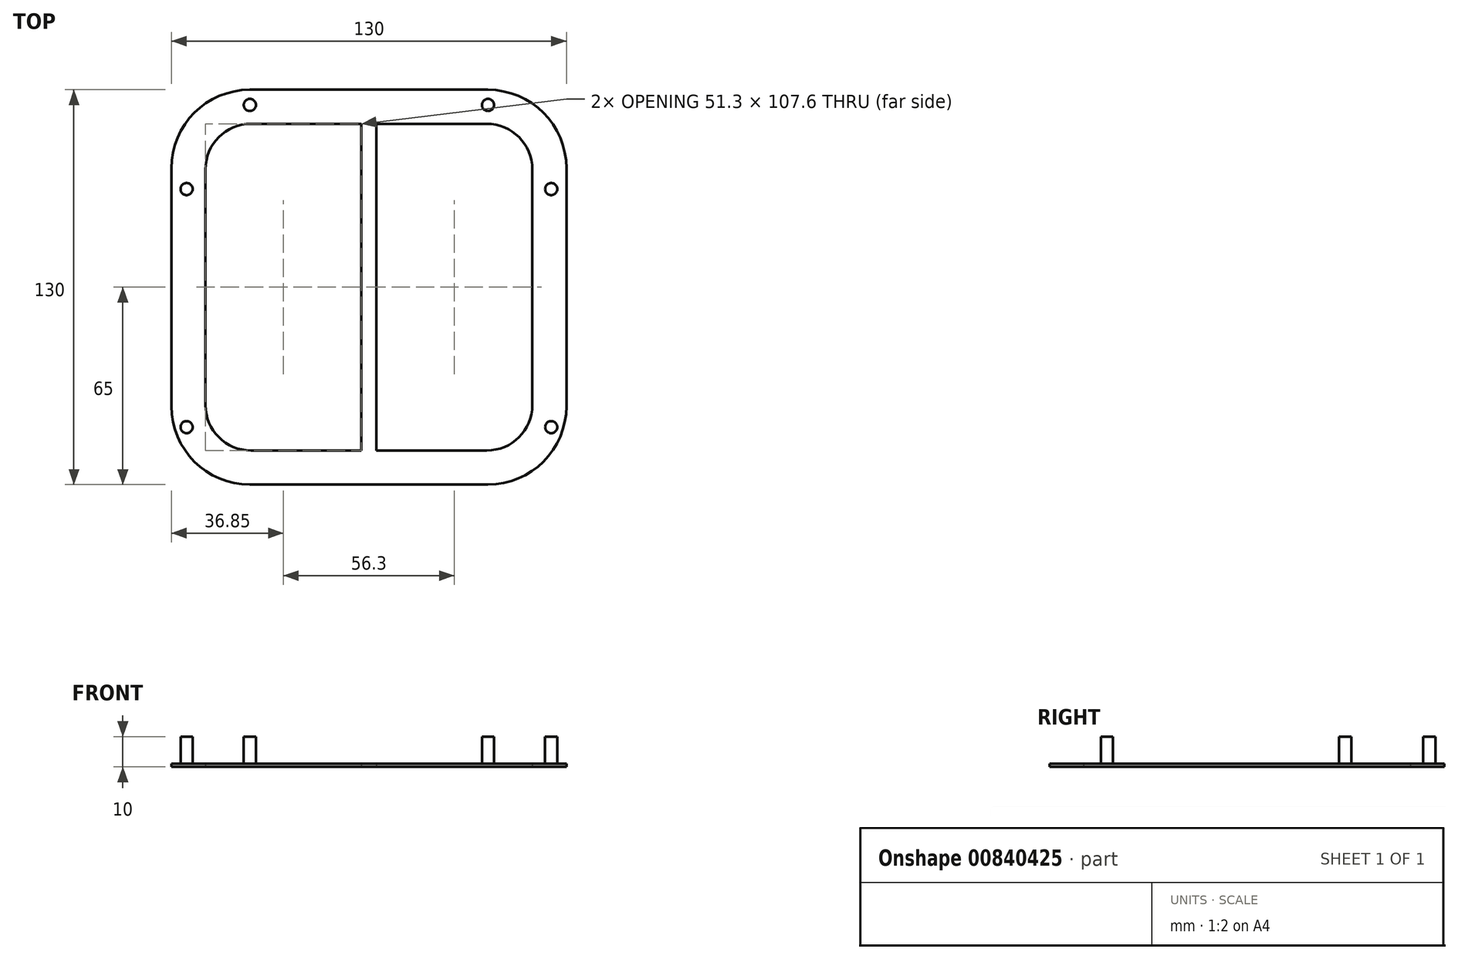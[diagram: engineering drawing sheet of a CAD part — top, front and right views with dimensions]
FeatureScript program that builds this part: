
annotation { "Feature Type Name" : "Feature", "Feature Type Description" : "" }
export const myFeature = defineFeature(function(context is Context, id is Id, definition is map)
    precondition{}
    {
        {
            var Q0;
            Q0=qCreatedBy(makeId("Top.planeOp"),FACE);
            var sketch = newSketch(context, id + "F0", { "sketchPlane" : qUnion([Q0])});
            skLineSegment(sketch, "E0.bottom", {"start": v(-39.2, 55) * mm, "end": v(39.2, 55) * mm});
            skLineSegment(sketch, "E0.top", {"start": v(-39.2, -55) * mm, "end": v(39.2, -55) * mm});
            skLineSegment(sketch, "E0.left", {"start": v(-55, 39.2) * mm, "end": v(-55, -39.2) * mm});
            skLineSegment(sketch, "E0.right", {"start": v(55, 39.2) * mm, "end": v(55, -39.2) * mm});
            skPoint(sketch, "E0.middle", {"position": v(0, 0) * mm});
            skLineSegment(sketch, "E1.bottom", {"start": v(39.2, 65) * mm, "end": v(-39.2, 65) * mm});
            skLineSegment(sketch, "E1.top", {"start": v(39.2, -65) * mm, "end": v(-39.2, -65) * mm});
            skLineSegment(sketch, "E1.left", {"start": v(65, 39.2) * mm, "end": v(65, -39.2) * mm});
            skLineSegment(sketch, "E1.right", {"start": v(-65, 39.2) * mm, "end": v(-65, -39.2) * mm});
            skLineSegment(sketch, "E2.0", {"start": v(-38.8, 53.8) * mm, "end": v(38.8, 53.8) * mm});
            skLineSegment(sketch, "E2.1", {"start": v(-53.8, 38.8) * mm, "end": v(-53.8, -38.8) * mm});
            skLineSegment(sketch, "E2.2", {"start": v(-38.8, -53.8) * mm, "end": v(38.8, -53.8) * mm});
            skLineSegment(sketch, "E2.3", {"start": v(53.8, 38.8) * mm, "end": v(53.8, -38.8) * mm});
            skPoint(sketch, "E3.visualSharp", {"position": v(-53.8, -53.8) * mm});
            skArc(sketch, "E3.filletArc", {"start": v(-53.8, -38.8) * mm, "mid": v(-49.4, -49.4) * mm, "end": v(-38.8, -53.8) * mm});
            skPoint(sketch, "E4.visualSharp", {"position": v(-55, -55) * mm});
            skArc(sketch, "E4.filletArc", {"start": v(-55, -39.2) * mm, "mid": v(-50.37, -50.37) * mm, "end": v(-39.2, -55) * mm});
            skPoint(sketch, "E5.visualSharp", {"position": v(53.8, -53.8) * mm});
            skArc(sketch, "E5.filletArc", {"start": v(38.8, -53.8) * mm, "mid": v(49.4, -49.4) * mm, "end": v(53.8, -38.8) * mm});
            skPoint(sketch, "E6.visualSharp", {"position": v(53.8, 53.8) * mm});
            skArc(sketch, "E6.filletArc", {"start": v(53.8, 38.8) * mm, "mid": v(49.4, 49.4) * mm, "end": v(38.8, 53.8) * mm});
            skPoint(sketch, "E7.visualSharp", {"position": v(-53.8, 53.8) * mm});
            skArc(sketch, "E7.filletArc", {"start": v(-38.8, 53.8) * mm, "mid": v(-49.4, 49.4) * mm, "end": v(-53.8, 38.8) * mm});
            skPoint(sketch, "E8.visualSharp", {"position": v(-55, 55) * mm});
            skArc(sketch, "E8.filletArc", {"start": v(-39.2, 55) * mm, "mid": v(-50.37, 50.37) * mm, "end": v(-55, 39.2) * mm});
            skPoint(sketch, "E9.visualSharp", {"position": v(55, 55) * mm});
            skArc(sketch, "E9.filletArc", {"start": v(55, 39.2) * mm, "mid": v(50.37, 50.37) * mm, "end": v(39.2, 55) * mm});
            skPoint(sketch, "E10.visualSharp", {"position": v(55, -55) * mm});
            skArc(sketch, "E10.filletArc", {"start": v(39.2, -55) * mm, "mid": v(50.37, -50.37) * mm, "end": v(55, -39.2) * mm});
            skPoint(sketch, "E11.visualSharp", {"position": v(65, -65) * mm});
            skArc(sketch, "E11.filletArc", {"start": v(39.2, -65) * mm, "mid": v(57.44, -57.44) * mm, "end": v(65, -39.2) * mm});
            skPoint(sketch, "E12.visualSharp", {"position": v(-65, -65) * mm});
            skArc(sketch, "E12.filletArc", {"start": v(-65, -39.2) * mm, "mid": v(-57.44, -57.44) * mm, "end": v(-39.2, -65) * mm});
            skPoint(sketch, "E13.visualSharp", {"position": v(65, 65) * mm});
            skArc(sketch, "E13.filletArc", {"start": v(65, 39.2) * mm, "mid": v(57.44, 57.44) * mm, "end": v(39.2, 65) * mm});
            skPoint(sketch, "E14.visualSharp", {"position": v(-65, 65) * mm});
            skArc(sketch, "E14.filletArc", {"start": v(-39.2, 65) * mm, "mid": v(-57.44, 57.44) * mm, "end": v(-65, 39.2) * mm});
            skLineSegment(sketch, "E15.0", {"start": v(60, 32.3) * mm, "end": v(60, -46.1) * mm});
            skLineSegment(sketch, "E16.0", {"start": v(-60, 32.3) * mm, "end": v(-60, -46.1) * mm});
            skCircle(sketch, "E17", {"center": v(60, 32.3) * mm, "radius": 2 * mm});
            skCircle(sketch, "E18", {"center": v(60, -46.1) * mm, "radius": 2 * mm});
            skCircle(sketch, "E19", {"center": v(-60, 32.3) * mm, "radius": 2 * mm});
            skCircle(sketch, "E20", {"center": v(-60, -46.1) * mm, "radius": 2 * mm});
            skLineSegment(sketch, "E21.0", {"start": v(39.2, 60) * mm, "end": v(-39.2, 60) * mm});
            skCircle(sketch, "E22", {"center": v(-39.2, 60) * mm, "radius": 2 * mm});
            skCircle(sketch, "E23", {"center": v(39.2, 60) * mm, "radius": 2 * mm});
            skLineSegment(sketch, "E24", {"start": v(-2.5, -55) * mm, "end": v(-2.5, 55) * mm});
            skLineSegment(sketch, "E25", {"start": v(2.5, 55) * mm, "end": v(2.5, -55) * mm});
            skLineSegment(sketch, "E26.0", {"start": v(1.3, 55) * mm, "end": v(1.3, -58.08) * mm});
            skLineSegment(sketch, "E27.0", {"start": v(-1.3, -55) * mm, "end": v(-1.3, 55) * mm});
            skSolve(sketch);
        }
        {
            var Q0;
            Q0=makeQuery(id+"F0.imprint","IMPRINT",FACE,{"disambiguationData":[TD([[makeQuery(id+"F0.imprint","IMPRINT",EDGE,{"derivedFrom":sQuery(id+"F0.wireOp",EDGE,"E0.left")}),1.0]])]});
            var Q1;
            {var subQ0=sQuery(id+"F0.wireOp",EDGE,"E24");var subQ1=sQuery(id+"F0.wireOp",EDGE,"E2.0");var subQ2=makeQuery(id+"F0.imprint","INTERSECT",VERTEX,{"derivedFrom":[subQ1,subQ0]});Q1=makeQuery(id+"F0.imprint","IMPRINT",FACE,{"disambiguationData":[TD([[makeQuery(id+"F0.imprint","IMPRINT",EDGE,{"disambiguationData":[TD([[subQ2,-1.0]])],"derivedFrom":subQ1}),-1.0]])]});}
            var Q2;
            {var subQ0=sQuery(id+"F0.wireOp",EDGE,"E24");var subQ1=sQuery(id+"F0.wireOp",EDGE,"E0.top");var subQ2=makeQuery(id+"F0.imprint","INTERSECT",VERTEX,{"derivedFrom":[subQ1,subQ0]});Q2=makeQuery(id+"F0.imprint","IMPRINT",FACE,{"disambiguationData":[TD([[makeQuery(id+"F0.imprint","IMPRINT",EDGE,{"disambiguationData":[TD([[subQ2,-1.0]])],"derivedFrom":subQ1}),1.0]])]});}
            var Q3;
            {var subQ0=sQuery(id+"F0.wireOp",EDGE,"E26.0");var subQ1=sQuery(id+"F0.wireOp",EDGE,"E0.top");var subQ2=makeQuery(id+"F0.imprint","INTERSECT",VERTEX,{"derivedFrom":[subQ1,subQ0]});Q3=makeQuery(id+"F0.imprint","IMPRINT",FACE,{"disambiguationData":[TD([[makeQuery(id+"F0.imprint","IMPRINT",EDGE,{"disambiguationData":[TD([[subQ2,1.0]])],"derivedFrom":subQ1}),1.0]])]});}
            var Q4;
            {var subQ0=sQuery(id+"F0.wireOp",EDGE,"E27.0");var subQ1=sQuery(id+"F0.wireOp",EDGE,"E2.0");var subQ2=makeQuery(id+"F0.imprint","INTERSECT",VERTEX,{"derivedFrom":[subQ1,subQ0]});Q4=makeQuery(id+"F0.imprint","IMPRINT",FACE,{"disambiguationData":[TD([[makeQuery(id+"F0.imprint","IMPRINT",EDGE,{"disambiguationData":[TD([[subQ2,-1.0]])],"derivedFrom":subQ1}),-1.0]])]});}
            var Q5;
            {var subQ0=sQuery(id+"F0.wireOp",EDGE,"E26.0");var subQ1=sQuery(id+"F0.wireOp",EDGE,"E2.0");var subQ2=makeQuery(id+"F0.imprint","INTERSECT",VERTEX,{"derivedFrom":[subQ1,subQ0]});Q5=makeQuery(id+"F0.imprint","IMPRINT",FACE,{"disambiguationData":[TD([[makeQuery(id+"F0.imprint","IMPRINT",EDGE,{"disambiguationData":[TD([[subQ2,-1.0]])],"derivedFrom":subQ1}),-1.0]])]});}
            var Q6;
            {var subQ0=sQuery(id+"F0.wireOp",EDGE,"E25");var subQ1=sQuery(id+"F0.wireOp",EDGE,"E0.top");var subQ2=makeQuery(id+"F0.imprint","INTERSECT",VERTEX,{"derivedFrom":[subQ1,subQ0]});Q6=makeQuery(id+"F0.imprint","IMPRINT",FACE,{"disambiguationData":[TD([[makeQuery(id+"F0.imprint","IMPRINT",EDGE,{"disambiguationData":[TD([[subQ2,1.0]])],"derivedFrom":subQ1}),1.0]])]});}
            var Q7;
            Q7=makeQuery(id+"F0.imprint","IMPRINT",FACE,{"disambiguationData":[TD([[makeQuery(id+"F0.imprint","IMPRINT",EDGE,{"derivedFrom":sQuery(id+"F0.wireOp",EDGE,"E0.right")}),-1.0]])]});
            var Q8;
            {var subQ0=sQuery(id+"F0.wireOp",EDGE,"E24");var subQ1=sQuery(id+"F0.wireOp",EDGE,"E0.bottom");var subQ2=makeQuery(id+"F0.imprint","INTERSECT",VERTEX,{"derivedFrom":[subQ1,subQ0]});Q8=makeQuery(id+"F0.imprint","IMPRINT",FACE,{"disambiguationData":[TD([[makeQuery(id+"F0.imprint","IMPRINT",EDGE,{"disambiguationData":[TD([[subQ2,-1.0]])],"derivedFrom":subQ1}),-1.0]])]});}
            var Q9;
            {var subQ0=sQuery(id+"F0.wireOp",EDGE,"E26.0");var subQ1=sQuery(id+"F0.wireOp",EDGE,"E0.bottom");var subQ2=makeQuery(id+"F0.imprint","INTERSECT",VERTEX,{"derivedFrom":[subQ1,subQ0]});Q9=makeQuery(id+"F0.imprint","IMPRINT",FACE,{"disambiguationData":[TD([[makeQuery(id+"F0.imprint","IMPRINT",EDGE,{"disambiguationData":[TD([[subQ2,1.0]])],"derivedFrom":subQ1}),-1.0]])]});}
            var Q10;
            {var subQ0=sQuery(id+"F0.wireOp",EDGE,"E25");var subQ1=sQuery(id+"F0.wireOp",EDGE,"E0.bottom");var subQ2=makeQuery(id+"F0.imprint","INTERSECT",VERTEX,{"derivedFrom":[subQ1,subQ0]});Q10=makeQuery(id+"F0.imprint","IMPRINT",FACE,{"disambiguationData":[TD([[makeQuery(id+"F0.imprint","IMPRINT",EDGE,{"disambiguationData":[TD([[subQ2,1.0]])],"derivedFrom":subQ1}),-1.0]])]});}
            var Q11;
            Q11=makeQuery(id+"F0.imprint","IMPRINT",FACE,{"disambiguationData":[TD([[makeQuery(id+"F0.imprint","IMPRINT",EDGE,{"derivedFrom":sQuery(id+"F0.wireOp",EDGE,"E20")}),1.0]])]});
            var Q12;
            Q12=makeQuery(id+"F0.imprint","IMPRINT",FACE,{"disambiguationData":[TD([[makeQuery(id+"F0.imprint","IMPRINT",EDGE,{"derivedFrom":sQuery(id+"F0.wireOp",EDGE,"E19")}),1.0]])]});
            var Q13;
            Q13=makeQuery(id+"F0.imprint","IMPRINT",FACE,{"disambiguationData":[TD([[makeQuery(id+"F0.imprint","IMPRINT",EDGE,{"derivedFrom":sQuery(id+"F0.wireOp",EDGE,"E22")}),1.0]])]});
            var Q14;
            Q14=makeQuery(id+"F0.imprint","IMPRINT",FACE,{"disambiguationData":[TD([[makeQuery(id+"F0.imprint","IMPRINT",EDGE,{"derivedFrom":sQuery(id+"F0.wireOp",EDGE,"E23")}),1.0]])]});
            var Q15;
            Q15=makeQuery(id+"F0.imprint","IMPRINT",FACE,{"disambiguationData":[TD([[makeQuery(id+"F0.imprint","IMPRINT",EDGE,{"derivedFrom":sQuery(id+"F0.wireOp",EDGE,"E17")}),1.0]])]});
            var Q16;
            Q16=makeQuery(id+"F0.imprint","IMPRINT",FACE,{"disambiguationData":[TD([[makeQuery(id+"F0.imprint","IMPRINT",EDGE,{"derivedFrom":sQuery(id+"F0.wireOp",EDGE,"E0.left")}),-1.0]])]});
            var Q17;
            Q17=makeQuery(id+"F0.imprint","IMPRINT",FACE,{"disambiguationData":[TD([[makeQuery(id+"F0.imprint","IMPRINT",EDGE,{"derivedFrom":sQuery(id+"F0.wireOp",EDGE,"E18")}),1.0]])]});
            extrude(context, id + "F1", {"entities" : qUnion([Q0, Q1, Q2, Q3, Q4, Q5, Q6, Q7, Q8, Q9, Q10, Q11, Q12, Q13, Q14, Q15, Q16, Q17]), "depth" : 1 * mm, "offsetDistance" : 25 * mm});
        }
        {
            var Q0;
            Q0=makeQuery(id+"F0.imprint","IMPRINT",FACE,{"disambiguationData":[TD([[makeQuery(id+"F0.imprint","IMPRINT",EDGE,{"derivedFrom":sQuery(id+"F0.wireOp",EDGE,"E20")}),1.0]])]});
            var Q1;
            Q1=makeQuery(id+"F0.imprint","IMPRINT",FACE,{"disambiguationData":[TD([[makeQuery(id+"F0.imprint","IMPRINT",EDGE,{"derivedFrom":sQuery(id+"F0.wireOp",EDGE,"E19")}),1.0]])]});
            var Q2;
            Q2=makeQuery(id+"F0.imprint","IMPRINT",FACE,{"disambiguationData":[TD([[makeQuery(id+"F0.imprint","IMPRINT",EDGE,{"derivedFrom":sQuery(id+"F0.wireOp",EDGE,"E23")}),1.0]])]});
            var Q3;
            Q3=makeQuery(id+"F0.imprint","IMPRINT",FACE,{"disambiguationData":[TD([[makeQuery(id+"F0.imprint","IMPRINT",EDGE,{"derivedFrom":sQuery(id+"F0.wireOp",EDGE,"E22")}),1.0]])]});
            var Q4;
            Q4=makeQuery(id+"F0.imprint","IMPRINT",FACE,{"disambiguationData":[TD([[makeQuery(id+"F0.imprint","IMPRINT",EDGE,{"derivedFrom":sQuery(id+"F0.wireOp",EDGE,"E18")}),1.0]])]});
            var Q5;
            Q5=makeQuery(id+"F0.imprint","IMPRINT",FACE,{"disambiguationData":[TD([[makeQuery(id+"F0.imprint","IMPRINT",EDGE,{"derivedFrom":sQuery(id+"F0.wireOp",EDGE,"E17")}),1.0]])]});
            extrude(context, id + "F2", {"entities" : qUnion([Q0, Q1, Q2, Q3, Q4, Q5]), "operationType" : NewBodyOperationType.ADD, "depth" : 10 * mm, "offsetDistance" : 25 * mm});
        }
    });
